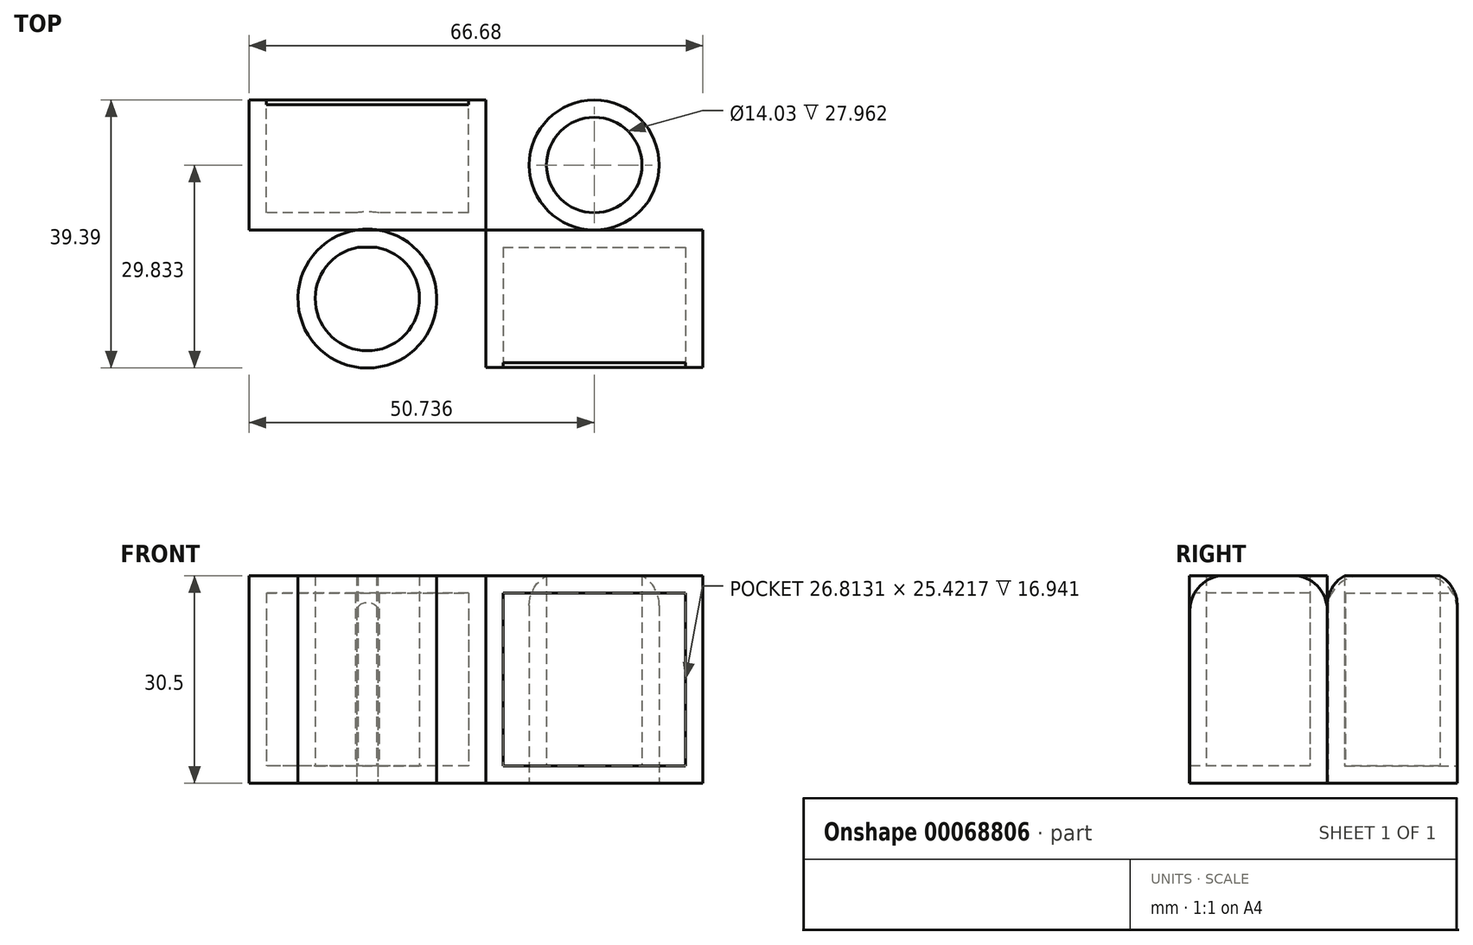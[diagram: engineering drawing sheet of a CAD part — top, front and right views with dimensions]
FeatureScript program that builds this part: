
annotation { "Feature Type Name" : "Feature", "Feature Type Description" : "" }
export const myFeature = defineFeature(function(context is Context, id is Id, definition is map)
    precondition{}
    {
        {
            var Q0;
            Q0=qCreatedBy(makeId("Top.planeOp"),FACE);
            var sketch = newSketch(context, id + "F0", { "sketchPlane" : qUnion([Q0])});
            skLineSegment(sketch, "E0.bottom", {"start": v(0, 0) * mm, "end": v(-34.8, 0) * mm});
            skLineSegment(sketch, "E0.top", {"start": v(0, 19.1) * mm, "end": v(-34.8, 19.1) * mm});
            skLineSegment(sketch, "E0.left", {"start": v(0, 0) * mm, "end": v(0, 19.1) * mm});
            skLineSegment(sketch, "E0.right", {"start": v(-34.8, 0) * mm, "end": v(-34.8, 19.1) * mm});
            skLineSegment(sketch, "E1.bottom", {"start": v(0, 0) * mm, "end": v(31.9, 0) * mm});
            skLineSegment(sketch, "E1.top", {"start": v(0, -20.16) * mm, "end": v(31.9, -20.16) * mm});
            skLineSegment(sketch, "E1.left", {"start": v(0, 0) * mm, "end": v(0, -20.16) * mm});
            skLineSegment(sketch, "E1.right", {"start": v(31.9, 0) * mm, "end": v(31.9, -20.16) * mm});
            skCircle(sketch, "E2", {"center": v(-17.4, -10.08) * mm, "radius": 10.2 * mm});
            skPoint(sketch, "E2.centerSnap0", {"position": v(0, -10.08) * mm});
            skPoint(sketch, "E2.centerSnap1", {"position": v(-17.4, 0) * mm});
            skCircle(sketch, "E3", {"center": v(15.95, 9.55) * mm, "radius": 9.55 * mm});
            skPoint(sketch, "E3.centerSnap0", {"position": v(0, 9.55) * mm});
            skPoint(sketch, "E3.centerSnap1", {"position": v(15.95, 0) * mm});
            skSolve(sketch);
        }
        {
            var Q0;
            Q0=makeQuery(id+"F0.imprint","IMPRINT",FACE,{"disambiguationData":[TD([[makeQuery(id+"F0.imprint","IMPRINT",EDGE,{"derivedFrom":sQuery(id+"F0.wireOp",EDGE,"E0.top")}),1.0]])]});
            var Q1;
            Q1=makeQuery(id+"F0.imprint","IMPRINT",FACE,{"disambiguationData":[TD([[makeQuery(id+"F0.imprint","IMPRINT",EDGE,{"derivedFrom":sQuery(id+"F0.wireOp",EDGE,"E3")}),1.0]])]});
            var Q2;
            Q2=makeQuery(id+"F0.imprint","IMPRINT",FACE,{"disambiguationData":[TD([[makeQuery(id+"F0.imprint","IMPRINT",EDGE,{"derivedFrom":sQuery(id+"F0.wireOp",EDGE,"E1.top")}),1.0]])]});
            var Q3;
            {var subQ0=sQuery(id+"F0.wireOp",EDGE,"E2");var subQ1=sQuery(id+"F0.wireOp",EDGE,"E0.bottom");var subQ2=makeQuery(id+"F0.imprint","INTERSECT",VERTEX,{"disambiguationData":[OD(0.0)],"derivedFrom":[subQ1,subQ0]});Q3=makeQuery(id+"F0.imprint","IMPRINT",FACE,{"disambiguationData":[TD([[makeQuery(id+"F0.imprint","IMPRINT",EDGE,{"disambiguationData":[TD([[subQ2,-1.0]])],"derivedFrom":subQ1}),1.0]])]});}
            extrude(context, id + "F1", {"entities" : qUnion([Q0, Q1, Q2, Q3]), "depth" : 30.5 * mm});
        }
        {
            var Q0;
            Q0=makeQuery(id+"F1.opExtrude","SWEPT_FACE",FACE,{"disambiguationData":[OSD([sQuery(id+"F0.wireOp",EDGE,"E1.top")])]});
            var Q1;
            Q1=makeQuery(id+"F1.opExtrude","SWEPT_FACE",FACE,{"disambiguationData":[OSD([sQuery(id+"F0.wireOp",EDGE,"E0.top")])]});
            shell(context, id + "F2", {"entities" : qUnion([Q0, Q1]), "thickness" : 2.54 * mm});
        }
        {
            var Q0;
            Q0=makeQuery(id+"F1.opExtrude","CAP_FACE",FACE,{"disambiguationData":[OSD([sQuery(id+"F0.wireOp",EDGE,"E0.bottom"),sQuery(id+"F0.wireOp",EDGE,"E2")])],"isStart":false});
            var Q1;
            Q1=makeQuery(id+"F1.opExtrude","CAP_FACE",FACE,{"disambiguationData":[OSD([sQuery(id+"F0.wireOp",EDGE,"E3")])],"isStart":false});
            shell(context, id + "F3", {"entities" : qUnion([Q0, Q1]), "thickness" : 2.54 * mm});
        }
        {
            var Q0;
            Q0=makeQuery(id+"F1.opExtrude","CAP_EDGE",EDGE,{"disambiguationData":[OSD([sQuery(id+"F0.wireOp",EDGE,"E1.top")])],"isStart":false});
            var Q1;
            Q1=makeQuery(id+"F1.opExtrude","CAP_EDGE",EDGE,{"disambiguationData":[OSD([sQuery(id+"F0.wireOp",EDGE,"E1.bottom")])],"isStart":false});
            var Q2;
            Q2=makeQuery(id+"F1.opExtrude","CAP_EDGE",EDGE,{"disambiguationData":[OSD([sQuery(id+"F0.wireOp",EDGE,"E0.top")])],"isStart":false});
            var Q3;
            Q3=makeQuery(id+"F1.opExtrude","CAP_EDGE",EDGE,{"disambiguationData":[OSD([sQuery(id+"F0.wireOp",EDGE,"E3")])],"isStart":false});
            var Q4;
            {var subQ0=sQuery(id+"F0.wireOp",EDGE,"E0.bottom");Q4=makeQuery(id+"F1.opExtrude","CAP_EDGE",EDGE,{"disambiguationData":[OSD([subQ0]),TDD([makeQuery(id+"F0.imprint","IMPRINT",EDGE,{"disambiguationData":[TD([[makeQuery(id+"F0.imprint","INTERSECT",VERTEX,{"derivedFrom":[subQ0,sQuery(id+"F0.wireOp",EDGE,"E0.right")]}),1.0]])],"derivedFrom":subQ0})])],"isStart":false});}
            fillet(context, id + "F4", {"entities" : qUnion([Q0, Q1, Q2, Q3, Q4]), "radius" : 5.08 * mm, "tangentPropagation" : true, "allowEdgeOverflow" : false});
        }
    });
